# Revit family: Reece_Seat_Wolfen_Shower Seat_600mm
name_source: partatom
category: Plumbing Fixtures
revit_build: Autodesk Revit 2018 (Build: 20190510_1515(x64)
units: mm (PartAtom-declared; Revit-internal decimal feet)

## family parameters
Always vertical = Yes
Cut with Voids When Loaded = Yes
Part Type = Normal
Room Calculation Point = No
Round Connector Dimension = Use Diameter
Shared = No
Work Plane-Based = Yes

## types (1)
- White_Stainless Steel
    Default Elevation = 0 mm  [stored 0 ft]
    Description = Wolfen Folding Shower Seat 600mm Stainless Steel & White
    Disclaimer = THIS FILE IS THE PROPERTY OF THE REECE GROUP. IT MAY NOT BE REPRODUCED, REVERSE-ENGINEERED OR MODIFIED. ANY REPUBLICATION, TRANSMISSION OR DISTRIBUTION FOR THE PURPOSE OF COMMERCIALLY EXPLOITING THE FILES IS PROHIBITED.
    Keynote = Product #2260056, Reece_Seat_Wolfen_Shower Seat_600mm - White_Stainless Steel
    Manufacturer = Wolfen
    Model = Wolfen
    Reece_Accessory_Projection = 785 mm
    Reece_Detail_Additional = Folding
    Reece_Detail_Disclaimer = THIS FILE IS THE PROPERTY OF THE REECE GROUP. IT MAY NOT BE REPRODUCED, REVERSE-ENGINEERED OR MODIFIED. ANY REPUBLICATION, TRANSMISSION OR DISTRIBUTION FOR THE PURPOSE OF COMMERCIALLY EXPLOITING THE FILES IS PROHIBITED.
    Reece_Material_Main = Reece_Plastic_White
    Reece_Material_Rubber = Reece_Brass_Rubber_Black
    Reece_Material_Secondary = Reece_Brass_Brushed Stainless Steel
    Reece_Overall_Height = 480 mm  [stored 1.5748 ft]
    Reece_Overall_Length = 360 mm  [stored 1.1811 ft]
    Reece_Overall_Width = 600 mm
    Reece_Product_Brand = Wolfen
    Reece_Product_Description = Wolfen Folding Shower Seat 600mm Stainless Steel & White
    Reece_Product_Mount = Wall Mounted
    Reece_Product_Number = 2260056
    Reece_Product_Sub Brand = Wolfen
    Reece_Product_Type = Seat
    Reece_Product_Web Page = https://www.reece.com.au
    Type Comments = Seat
    URL = https://www.reece.com.au

note: [stored X ft] marks values corroborated as IEEE doubles in the binary element streams (Revit-internal decimal feet)

## geometry (parser evidence)
native form markers: Sweep x7
no freeform markers — native parametric forms only
